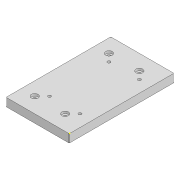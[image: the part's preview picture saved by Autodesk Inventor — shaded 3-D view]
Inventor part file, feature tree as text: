
AUTODESK INVENTOR PART (.ipt)
format: ipt  version: 2020 (Build 240168000, 168)  size: 224,768 bytes
history: native  units: mm
features: sketch x8, extrude x7, other x4, fillet x1
ambient origin geometry x8: Origin, YZ Plane, XZ Plane, XY Plane, X Axis, Y Axis, Z Axis, Center Point
bodies: Body1 (feature_tree)
feature tree (20):
  other  "Sólido1"
  extrude  "Extrusão1"  Depth=140.0mm
  extrude  "Extrusão2"  Depth=4.3mm
  sketch  "Esboço3"  dims[d4=4.3mm d5=4.3mm]
  extrude  "Extrusão3"  Depth=4.3mm
  extrude  "Extrusão4"  Depth=10.0mm
  extrude  "Extrusão5"  Depth=20.0mm
  extrude  "Extrusão6"  Depth=20.0mm
  extrude  "Extrusão7"  Depth=11.0mm
  fillet  "Arredondamento1"  Radius=11.0mm
  sketch  "Esboço1"  dims[d0=77.0mm d1=140.0mm]
  sketch  "Esboço2"  dims[d2=4.3mm d3=4.3mm]
  sketch  "Esboço4"  dims[d6=10.0mm d7=10.0mm]
  sketch  "Esboço5"  dims[d8=20.0mm d9=20.0mm]
  sketch  "Esboço6"  dims[d10=20.0mm d11=20.0mm]
  other  "Contorno projetado1"
  sketch  "Esboço7"  dims[d12=26.0mm d13=26.0mm d14=11.0mm d15=0.0mm]
  other  "Contorno projetado2"
  sketch  "Esboço8"  dims[d16=9.0mm d17=9.0mm d18=9.0mm d19=9.0mm d20=3.0mm d21=0.0mm d22=4.0mm d23=4.0mm d24=10.0mm d25=10.0mm d26=10.0mm d27=10.0mm d28=4.0mm d29=4.0mm d30=10.0mm d31=10.0mm d32=10.0mm d33=10.0mm d34=12.0mm d35=0.0mm d36=6.95mm d37=6.95mm d38=6.95mm d39=6.95mm d40=6.0mm d41=0.0mm d42=0.5mm d43=0.0mm d44=0.5mm d45=0.0mm d46=8.0mm d47=0.0mm d48=1.0mm]
  other  "Contorno projetado3"
